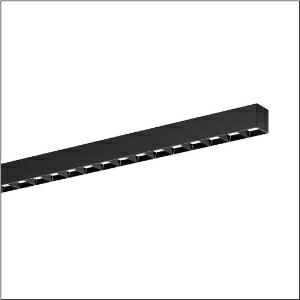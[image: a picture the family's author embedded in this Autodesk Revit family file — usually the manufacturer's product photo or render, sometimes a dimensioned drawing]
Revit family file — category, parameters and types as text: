
# Revit family: silica_r__21_51mx24dc3abb_157e
name_source: partatom
category: Lighting Fixtures
units: mm (PartAtom-declared; Revit-internal decimal feet)

## family parameters
Cut with Voids When Loaded = No
Host = Face
Light Source = No
Part Type = Normal
Room Calculation Point = No
Round Connector Dimension = Use Diameter
Shared = No

## types (1)
- --- (1 x LED, 10800 lm, 79 W, 3000K)
    Apparent Load = 79 VA
    CIE Flux Codes = 74 94 99 100 100
    Color Rendering = 80
    Color Temperature = 3000K
    Default Elevation = 1800 mm
    Description = Silica® 21, office luminaire, primary light control with darklight reflector, of PMMA, black, CAT 2 (L<= 3000cd/m²), light emission: direct distribution, primary light characteristic: asymmetric, installation type: surface-mounted, LED, rated luminous flux: 10.800lm, luminous efficacy: 137lm/W, light colour: 830, colour temperature: 3000K, with terminal, 3+2-pole, max. 2.5mm², mains connection: 220..240V, AC, 50/60Hz, rated input power: 79W, luminaire housing, of aluminium, jet black (RAL 9005), length: 3.004mm, width: 53mm, height: 53mm, protection rating (complete): IP20, insulation class (complete): insulation class I (protective earthing), certification: CE, permissible operating ambient temperature: 0..+35°C, standard: EN 50419, packaging unit: 1 piece
    Height = 0 mm  [stored 0 ft]
    Lamp = 1 x LED
    Lamp Light Flux = 10800 lm
    Lamp Power = 79 W
    Lamp count = 1
    Length = 3004 mm
    Luminous efficacy = 137 lm/W
    Manufacturer = Siteco
    ModVariant = No
    Model = 51MX24DC3ABB
    Mounting Place = Ceiling
    Mounting Type = Recessed
    Number of Poles = 1
    OnlyDefault = Yes
    Power Factor = 1
    Product Name = Silica® 21
    Product group = office luminaire | ceiling recessed
    ProductGroupID = 400
    Protection Class = Protection class I
    Protection Degree = IP 20
    RLX_Detail_Level = 1
    RLX_Emergency_Light_Flux = 0 lm
    RLX_Emergency_Type = 0
    RLX_Emergency_Type_DB = No
    RlxData = <blob elided: 66677 chars, md5=77947d0e>
    Socket = socket
    Standby Power = 0 W
    System Light Flux = 10800 lm
    System Power = 79 W
    Type Comments = factory setting: luminous flux: 100 % | dim-lin: 254 | 448 mA
    Type Image = l_1335908.jpg
    URL = http://relux.com
    VarID = @adj_092327
    Voltage = 0 V
    Weight = 0.00 kg
    Width = 53 mm

note: [stored X ft] marks values corroborated as IEEE doubles in the binary element streams (Revit-internal decimal feet)

## geometry (parser evidence)
native form markers: Blend x4, Sweep x10
no freeform markers — native parametric forms only
